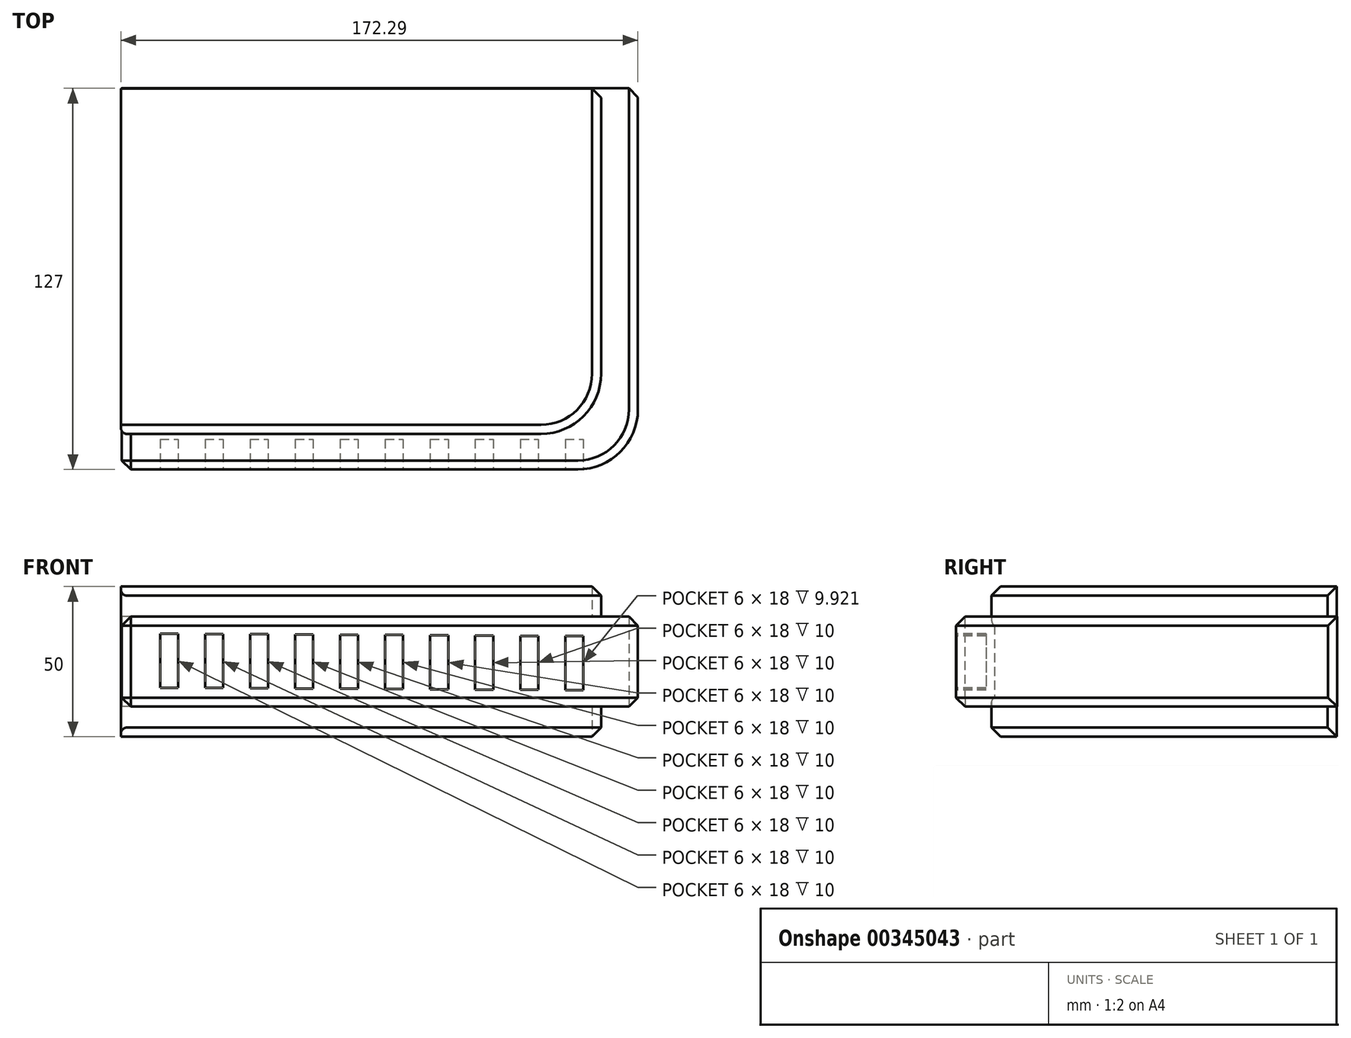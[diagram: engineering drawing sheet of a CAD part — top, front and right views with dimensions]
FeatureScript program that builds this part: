
annotation { "Feature Type Name" : "Feature", "Feature Type Description" : "" }
export const myFeature = defineFeature(function(context is Context, id is Id, definition is map)
    precondition{}
    {
        {
            var Q0;
            Q0=qCreatedBy(makeId("Top.planeOp"),FACE);
            var sketch = newSketch(context, id + "F0", { "sketchPlane" : qUnion([Q0])});
            skLineSegment(sketch, "E0.bottom", {"start": v(86, -63.5) * mm, "end": v(-86, -63.5) * mm});
            skLineSegment(sketch, "E0.top", {"start": v(86, 63.5) * mm, "end": v(-86, 63.5) * mm});
            skLineSegment(sketch, "E0.left", {"start": v(86, -63.5) * mm, "end": v(86, 63.5) * mm});
            skLineSegment(sketch, "E0.right", {"start": v(-86, -63.5) * mm, "end": v(-86, 63.5) * mm});
            skPoint(sketch, "E0.middle", {"position": v(0, 0) * mm});
            skSolve(sketch);
        }
        {
            var Q0;
            Q0 = qSketchRegion(id + "F0", true);
            extrude(context, id + "F1", {"entities" : qUnion([Q0]), "depth" : 15 * mm, "hasSecondDirection" : true, "secondDirectionOppositeDirection" : true, "secondDirectionDepth" : 15 * mm});
        }
        {
            var Q0;
            Q0=qCreatedBy(makeId("Top.planeOp"),FACE);
            var sketch = newSketch(context, id + "F2", { "sketchPlane" : qUnion([Q0])});
            skLineSegment(sketch, "E1.bottom", {"start": v(-86.29, 63.35) * mm, "end": v(73.71, 63.35) * mm});
            skLineSegment(sketch, "E1.top", {"start": v(-86.29, -51.65) * mm, "end": v(73.71, -51.65) * mm});
            skLineSegment(sketch, "E1.left", {"start": v(-86.29, 63.35) * mm, "end": v(-86.29, -51.65) * mm});
            skLineSegment(sketch, "E1.right", {"start": v(73.71, 63.35) * mm, "end": v(73.71, -51.65) * mm});
            skSolve(sketch);
        }
        {
            var Q0;
            Q0 = qSketchRegion(id + "F2", true);
            extrude(context, id + "F3", {"entities" : qUnion([Q0]), "operationType" : NewBodyOperationType.ADD, "depth" : 25 * mm, "hasSecondDirection" : true, "secondDirectionOppositeDirection" : true, "secondDirectionDepth" : 25 * mm});
        }
        {
            var Q0;
            {var subQ0=sQuery(id+"F2.wireOp",EDGE,"E1.right");var subQ1=sQuery(id+"F2.wireOp",EDGE,"E1.top");Q0=makeQuery(id+"F3.boolean.opBoolean","SPLIT",EDGE,{"disambiguationData":[TD([makeQuery(id+"F1.opExtrude","CAP_FACE",FACE,{"disambiguationData":[OSD([sQuery(id+"F0.wireOp",EDGE,"E0.bottom"),sQuery(id+"F0.wireOp",EDGE,"E0.top"),sQuery(id+"F0.wireOp",EDGE,"E0.left"),sQuery(id+"F0.wireOp",EDGE,"E0.right")])],"isStart":false})])],"derivedFrom":makeQuery(id+"F3.opExtrude","SWEPT_EDGE",EDGE,{"disambiguationData":[OSD([subQ1,subQ0])]})});}
            var Q1;
            Q1=makeQuery(id+"F1.opExtrude","SWEPT_EDGE",EDGE,{"disambiguationData":[OSD([sQuery(id+"F0.wireOp",EDGE,"E0.bottom"),sQuery(id+"F0.wireOp",EDGE,"E0.left")])]});
            var Q2;
            {var subQ0=sQuery(id+"F2.wireOp",EDGE,"E1.top");var subQ1=sQuery(id+"F2.wireOp",EDGE,"E1.right");Q2=makeQuery(id+"F3.boolean.opBoolean","SPLIT",EDGE,{"disambiguationData":[TD([makeQuery(id+"F1.opExtrude","CAP_FACE",FACE,{"disambiguationData":[OSD([sQuery(id+"F0.wireOp",EDGE,"E0.bottom"),sQuery(id+"F0.wireOp",EDGE,"E0.top"),sQuery(id+"F0.wireOp",EDGE,"E0.left"),sQuery(id+"F0.wireOp",EDGE,"E0.right")])],"isStart":true})])],"derivedFrom":makeQuery(id+"F3.opExtrude","SWEPT_EDGE",EDGE,{"disambiguationData":[OSD([subQ0,subQ1])]})});}
            fillet(context, id + "F4", {"entities" : qUnion([Q0, Q1, Q2]), "radius" : 20 * mm, "tangentPropagation" : true, "allowEdgeOverflow" : false});
        }
        {
            var Q0;
            Q0=makeQuery(id+"F3.opExtrude","CAP_EDGE",EDGE,{"disambiguationData":[OSD([sQuery(id+"F2.wireOp",EDGE,"E1.top")])],"isStart":false});
            var Q1;
            Q1=makeQuery(id+"F1.opExtrude","CAP_EDGE",EDGE,{"disambiguationData":[OSD([sQuery(id+"F0.wireOp",EDGE,"E0.bottom")])],"isStart":false});
            var Q2;
            Q2=makeQuery(id+"F1.opExtrude","CAP_EDGE",EDGE,{"disambiguationData":[OSD([sQuery(id+"F0.wireOp",EDGE,"E0.bottom")])],"isStart":true});
            var Q3;
            Q3=makeQuery(id+"F3.opExtrude","CAP_EDGE",EDGE,{"disambiguationData":[OSD([sQuery(id+"F2.wireOp",EDGE,"E1.top")])],"isStart":true});
            var Q4;
            Q4=makeQuery(id+"F1.opExtrude","SWEPT_EDGE",EDGE,{"disambiguationData":[OSD([sQuery(id+"F0.wireOp",EDGE,"E0.top"),sQuery(id+"F0.wireOp",EDGE,"E0.left")])]});
            var Q5;
            {var subQ0=sQuery(id+"F2.wireOp",EDGE,"E1.bottom");var subQ1=sQuery(id+"F2.wireOp",EDGE,"E1.right");Q5=makeQuery(id+"F3.boolean.opBoolean","SPLIT",EDGE,{"disambiguationData":[TD([makeQuery(id+"F1.opExtrude","CAP_FACE",FACE,{"disambiguationData":[OSD([sQuery(id+"F0.wireOp",EDGE,"E0.bottom"),sQuery(id+"F0.wireOp",EDGE,"E0.top"),sQuery(id+"F0.wireOp",EDGE,"E0.left"),sQuery(id+"F0.wireOp",EDGE,"E0.right")])],"isStart":false})])],"derivedFrom":makeQuery(id+"F3.opExtrude","SWEPT_EDGE",EDGE,{"disambiguationData":[OSD([subQ0,subQ1])]})});}
            var Q6;
            {var subQ0=sQuery(id+"F2.wireOp",EDGE,"E1.bottom");var subQ1=sQuery(id+"F2.wireOp",EDGE,"E1.right");Q6=makeQuery(id+"F3.boolean.opBoolean","SPLIT",EDGE,{"disambiguationData":[TD([makeQuery(id+"F1.opExtrude","CAP_FACE",FACE,{"disambiguationData":[OSD([sQuery(id+"F0.wireOp",EDGE,"E0.bottom"),sQuery(id+"F0.wireOp",EDGE,"E0.top"),sQuery(id+"F0.wireOp",EDGE,"E0.left"),sQuery(id+"F0.wireOp",EDGE,"E0.right")])],"isStart":true})])],"derivedFrom":makeQuery(id+"F3.opExtrude","SWEPT_EDGE",EDGE,{"disambiguationData":[OSD([subQ0,subQ1])]})});}
            var Q7;
            Q7=makeQuery(id+"F1.opExtrude","SWEPT_EDGE",EDGE,{"disambiguationData":[OSD([sQuery(id+"F0.wireOp",EDGE,"E0.bottom"),sQuery(id+"F0.wireOp",EDGE,"E0.right")])]});
            var Q8;
            {var subQ0=sQuery(id+"F0.wireOp",EDGE,"E0.bottom");var subQ1=sQuery(id+"F0.wireOp",EDGE,"E0.right");Q8=makeQuery(id+"F3.boolean.opBoolean","SPLIT",EDGE,{"disambiguationData":[TD([makeQuery(id+"F1.opExtrude","SWEPT_FACE",FACE,{"disambiguationData":[OSD([subQ0])]})])],"derivedFrom":makeQuery(id+"F1.opExtrude","CAP_EDGE",EDGE,{"disambiguationData":[OSD([subQ1])],"isStart":false})});}
            var Q9;
            {var subQ0=sQuery(id+"F0.wireOp",EDGE,"E0.bottom");var subQ1=sQuery(id+"F0.wireOp",EDGE,"E0.right");Q9=makeQuery(id+"F3.boolean.opBoolean","SPLIT",EDGE,{"disambiguationData":[TD([makeQuery(id+"F1.opExtrude","SWEPT_FACE",FACE,{"disambiguationData":[OSD([subQ0])]})])],"derivedFrom":makeQuery(id+"F1.opExtrude","CAP_EDGE",EDGE,{"disambiguationData":[OSD([subQ1])],"isStart":true})});}
            chamfer(context, id + "F5", {"entities" : qUnion([Q0, Q1, Q2, Q3, Q4, Q5, Q6, Q7, Q8, Q9]), "width" : 3 * mm, "tangentPropagation" : true});
        }
        {
            var Q0;
            Q0=makeQuery(id+"F3.opExtrude","SWEPT_EDGE",EDGE,{"disambiguationData":[OSD([sQuery(id+"F2.wireOp",EDGE,"E1.top"),sQuery(id+"F2.wireOp",EDGE,"E1.left")])]});
            fillet(context, id + "F6", {"entities" : qUnion([Q0]), "radius" : 2 * mm, "tangentPropagation" : true, "allowEdgeOverflow" : false});
        }
        {
            var Q0;
            Q0=makeQuery(id+"F1.opExtrude","SWEPT_FACE",FACE,{"disambiguationData":[OSD([sQuery(id+"F0.wireOp",EDGE,"E0.bottom")])]});
            var sketch = newSketch(context, id + "F7", { "sketchPlane" : qUnion([Q0])});
            skLineSegment(sketch, "E2.bottom", {"start": v(-73.22, 9.29) * mm, "end": v(-67.22, 9.29) * mm});
            skLineSegment(sketch, "E2.top", {"start": v(-73.22, -8.71) * mm, "end": v(-67.22, -8.71) * mm});
            skLineSegment(sketch, "E2.left", {"start": v(-73.22, 9.29) * mm, "end": v(-73.22, -8.71) * mm});
            skLineSegment(sketch, "E2.right", {"start": v(-67.22, 9.29) * mm, "end": v(-67.22, -8.71) * mm});
            skLineSegment(sketch, "E3.1.0.0", {"start": v(-52.22, 9.2) * mm, "end": v(-52.22, -8.8) * mm});
            skLineSegment(sketch, "E3.1.0.1", {"start": v(-58.22, 9.2) * mm, "end": v(-52.22, 9.2) * mm});
            skLineSegment(sketch, "E3.1.0.2", {"start": v(-58.22, 9.2) * mm, "end": v(-58.22, -8.8) * mm});
            skLineSegment(sketch, "E3.1.0.3", {"start": v(-58.22, -8.8) * mm, "end": v(-52.22, -8.8) * mm});
            skLineSegment(sketch, "E3.2.0.0", {"start": v(-37.22, 9.11) * mm, "end": v(-37.22, -8.89) * mm});
            skLineSegment(sketch, "E3.2.0.1", {"start": v(-43.22, 9.11) * mm, "end": v(-37.22, 9.11) * mm});
            skLineSegment(sketch, "E3.2.0.2", {"start": v(-43.22, 9.11) * mm, "end": v(-43.22, -8.89) * mm});
            skLineSegment(sketch, "E3.2.0.3", {"start": v(-43.22, -8.89) * mm, "end": v(-37.22, -8.89) * mm});
            skLineSegment(sketch, "E3.3.0.0", {"start": v(-22.22, 9.02) * mm, "end": v(-22.22, -8.98) * mm});
            skLineSegment(sketch, "E3.3.0.1", {"start": v(-28.22, 9.02) * mm, "end": v(-22.22, 9.02) * mm});
            skLineSegment(sketch, "E3.3.0.2", {"start": v(-28.22, 9.02) * mm, "end": v(-28.22, -8.98) * mm});
            skLineSegment(sketch, "E3.3.0.3", {"start": v(-28.22, -8.98) * mm, "end": v(-22.22, -8.98) * mm});
            skLineSegment(sketch, "E3.4.0.0", {"start": v(-7.22, 8.94) * mm, "end": v(-7.22, -9.06) * mm});
            skLineSegment(sketch, "E3.4.0.1", {"start": v(-13.22, 8.94) * mm, "end": v(-7.22, 8.94) * mm});
            skLineSegment(sketch, "E3.4.0.2", {"start": v(-13.22, 8.94) * mm, "end": v(-13.22, -9.06) * mm});
            skLineSegment(sketch, "E3.4.0.3", {"start": v(-13.22, -9.06) * mm, "end": v(-7.22, -9.06) * mm});
            skLineSegment(sketch, "E3.5.0.0", {"start": v(7.78, 8.85) * mm, "end": v(7.78, -9.15) * mm});
            skLineSegment(sketch, "E3.5.0.1", {"start": v(1.78, 8.85) * mm, "end": v(7.78, 8.85) * mm});
            skLineSegment(sketch, "E3.5.0.2", {"start": v(1.78, 8.85) * mm, "end": v(1.78, -9.15) * mm});
            skLineSegment(sketch, "E3.5.0.3", {"start": v(1.78, -9.15) * mm, "end": v(7.78, -9.15) * mm});
            skLineSegment(sketch, "E3.6.0.0", {"start": v(22.78, 8.76) * mm, "end": v(22.78, -9.24) * mm});
            skLineSegment(sketch, "E3.6.0.1", {"start": v(16.78, 8.76) * mm, "end": v(22.78, 8.76) * mm});
            skLineSegment(sketch, "E3.6.0.2", {"start": v(16.78, 8.76) * mm, "end": v(16.78, -9.24) * mm});
            skLineSegment(sketch, "E3.6.0.3", {"start": v(16.78, -9.24) * mm, "end": v(22.78, -9.24) * mm});
            skLineSegment(sketch, "E3.7.0.0", {"start": v(37.78, 8.67) * mm, "end": v(37.78, -9.33) * mm});
            skLineSegment(sketch, "E3.7.0.1", {"start": v(31.78, 8.67) * mm, "end": v(37.78, 8.67) * mm});
            skLineSegment(sketch, "E3.7.0.2", {"start": v(31.78, 8.67) * mm, "end": v(31.78, -9.33) * mm});
            skLineSegment(sketch, "E3.7.0.3", {"start": v(31.78, -9.33) * mm, "end": v(37.78, -9.33) * mm});
            skLineSegment(sketch, "E3.8.0.0", {"start": v(52.78, 8.58) * mm, "end": v(52.78, -9.42) * mm});
            skLineSegment(sketch, "E3.8.0.1", {"start": v(46.78, 8.58) * mm, "end": v(52.78, 8.58) * mm});
            skLineSegment(sketch, "E3.8.0.2", {"start": v(46.78, 8.58) * mm, "end": v(46.78, -9.42) * mm});
            skLineSegment(sketch, "E3.8.0.3", {"start": v(46.78, -9.42) * mm, "end": v(52.78, -9.42) * mm});
            skLineSegment(sketch, "E3.9.0.0", {"start": v(67.78, 8.5) * mm, "end": v(67.78, -9.5) * mm});
            skLineSegment(sketch, "E3.9.0.1", {"start": v(61.78, 8.5) * mm, "end": v(67.78, 8.5) * mm});
            skLineSegment(sketch, "E3.9.0.2", {"start": v(61.78, 8.5) * mm, "end": v(61.78, -9.5) * mm});
            skLineSegment(sketch, "E3.9.0.3", {"start": v(61.78, -9.5) * mm, "end": v(67.78, -9.5) * mm});
            skLineSegment(sketch, "E3.direction1", {"start": v(-67.22, -8.71) * mm, "end": v(-52.22, -8.8) * mm, "construction": true});
            skSolve(sketch);
        }
        {
            var Q0;
            Q0 = qSketchRegion(id + "F7", true);
            var Q1;
            Q1=sQuery(id+"F7.wireOp",EDGE,"E3.4.0.0");
            var Q2;
            Q2=sQuery(id+"F7.wireOp",EDGE,"E3.4.0.3");
            var Q3;
            Q3=sQuery(id+"F7.wireOp",EDGE,"E3.4.0.2");
            var Q4;
            Q4=sQuery(id+"F7.wireOp",EDGE,"E3.4.0.1");
            var Q5;
            Q5=makeQuery(id+"F1.opExtrude","SWEPT_BODY",BODY,{"disambiguationData":[OSD([sQuery(id+"F0.wireOp",EDGE,"E0.bottom"),sQuery(id+"F0.wireOp",EDGE,"E0.top"),sQuery(id+"F0.wireOp",EDGE,"E0.left"),sQuery(id+"F0.wireOp",EDGE,"E0.right")])]});
            extrude(context, id + "F8", {"entities" : qUnion([Q0]), "operationType" : NewBodyOperationType.REMOVE, "surfaceEntities" : qUnion([Q1, Q2, Q3, Q4]), "oppositeDirection" : true, "endBoundEntityBody" : qUnion([Q5]), "depth" : 10 * mm});
        }
    });
